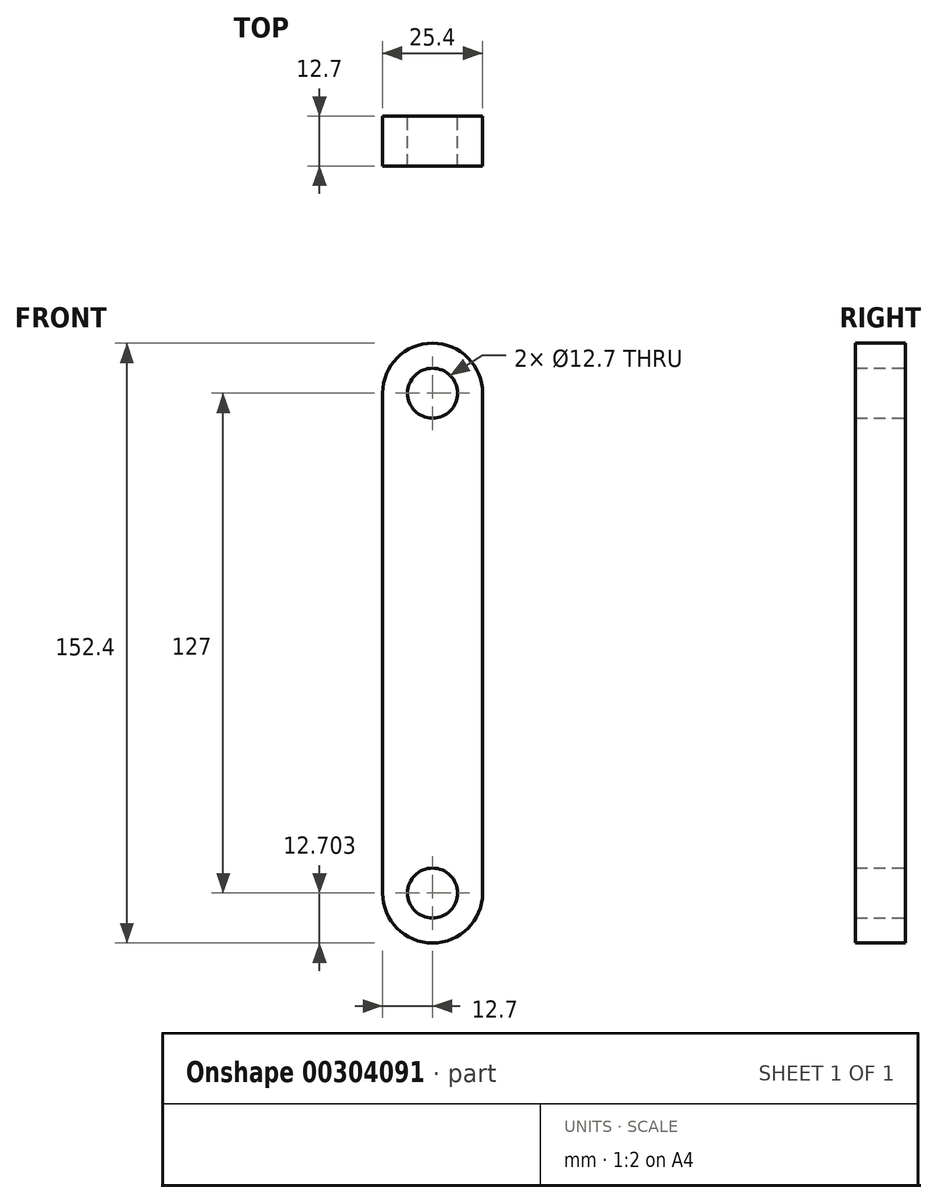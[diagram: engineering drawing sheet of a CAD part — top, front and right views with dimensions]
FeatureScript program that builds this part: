
annotation { "Feature Type Name" : "Feature", "Feature Type Description" : "" }
export const myFeature = defineFeature(function(context is Context, id is Id, definition is map)
    precondition{}
    {
        {
            var Q0;
            Q0=qCreatedBy(makeId("Front.planeOp"),FACE);
            var sketch = newSketch(context, id + "F0", { "sketchPlane" : qUnion([Q0])});
            skCircle(sketch, "E0", {"center": v(0, 114.56) * mm, "radius": 12.7 * mm});
            skCircle(sketch, "E1", {"center": v(0, -12.44) * mm, "radius": 12.7 * mm});
            skLineSegment(sketch, "E2", {"start": v(12.7, 114.56) * mm, "end": v(12.7, -12.44) * mm});
            skCircle(sketch, "E3", {"center": v(0, 114.56) * mm, "radius": 6.35 * mm});
            skCircle(sketch, "E4", {"center": v(0, -12.44) * mm, "radius": 6.35 * mm});
            skLineSegment(sketch, "E5", {"start": v(-12.7, -12.44) * mm, "end": v(-12.7, 114.56) * mm});
            skSolve(sketch);
        }
        {
            var Q0;
            Q0 = qSketchRegion(id + "F0", true);
            extrude(context, id + "F1", {"entities" : qUnion([Q0]), "endBound" : BoundingType.SYMMETRIC, "depth" : 12.7 * mm});
        }
    });
